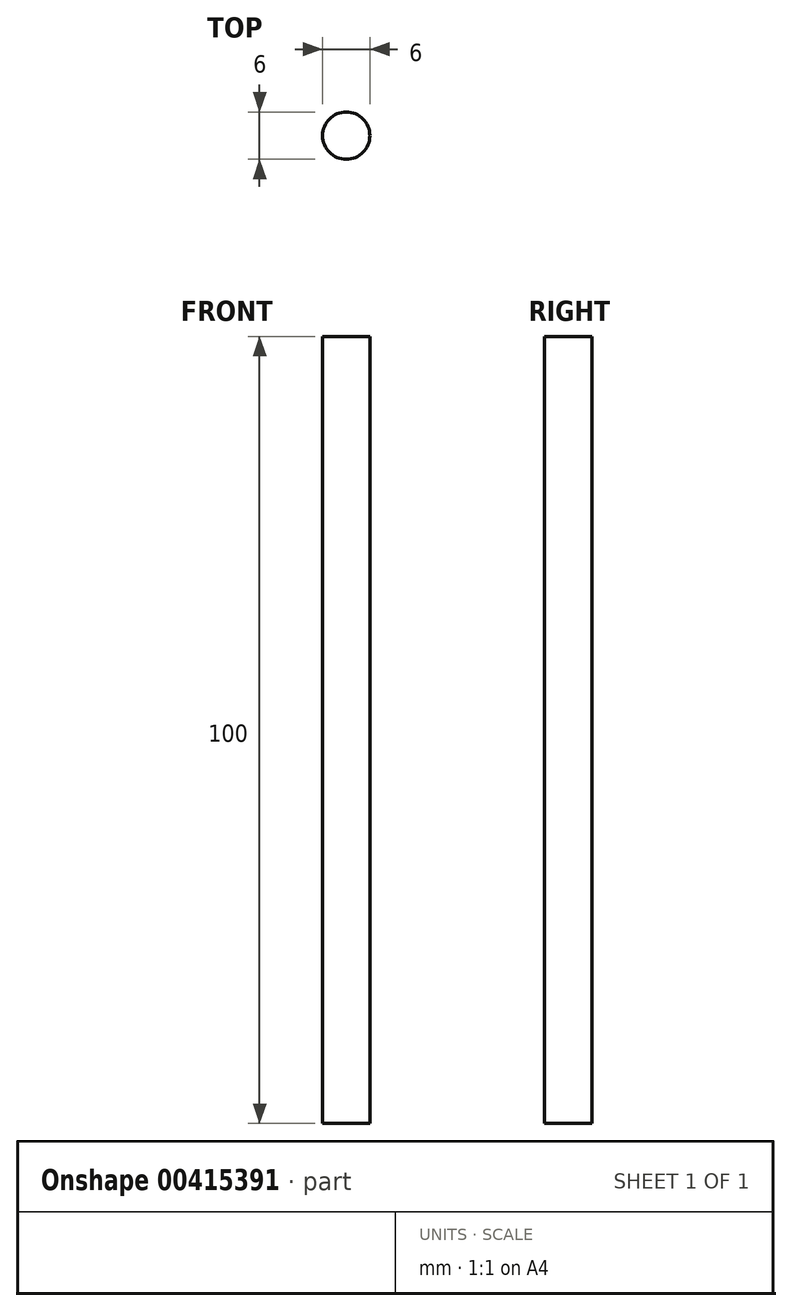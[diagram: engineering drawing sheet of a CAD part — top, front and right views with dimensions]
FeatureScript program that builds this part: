
annotation { "Feature Type Name" : "Feature", "Feature Type Description" : "" }
export const myFeature = defineFeature(function(context is Context, id is Id, definition is map)
    precondition{}
    {
        {
            var Q0;
            Q0=qCreatedBy(makeId("Top.planeOp"),FACE);
            var sketch = newSketch(context, id + "F0", { "sketchPlane" : qUnion([Q0])});
            skCircle(sketch, "E0", {"center": v(0, 0) * mm, "radius": 3 * mm});
            skSolve(sketch);
        }
        {
            var Q0;
            Q0 = qSketchRegion(id + "F0", true);
            extrude(context, id + "F1", {"entities" : qUnion([Q0]), "depth" : 100 * mm});
        }
    });
